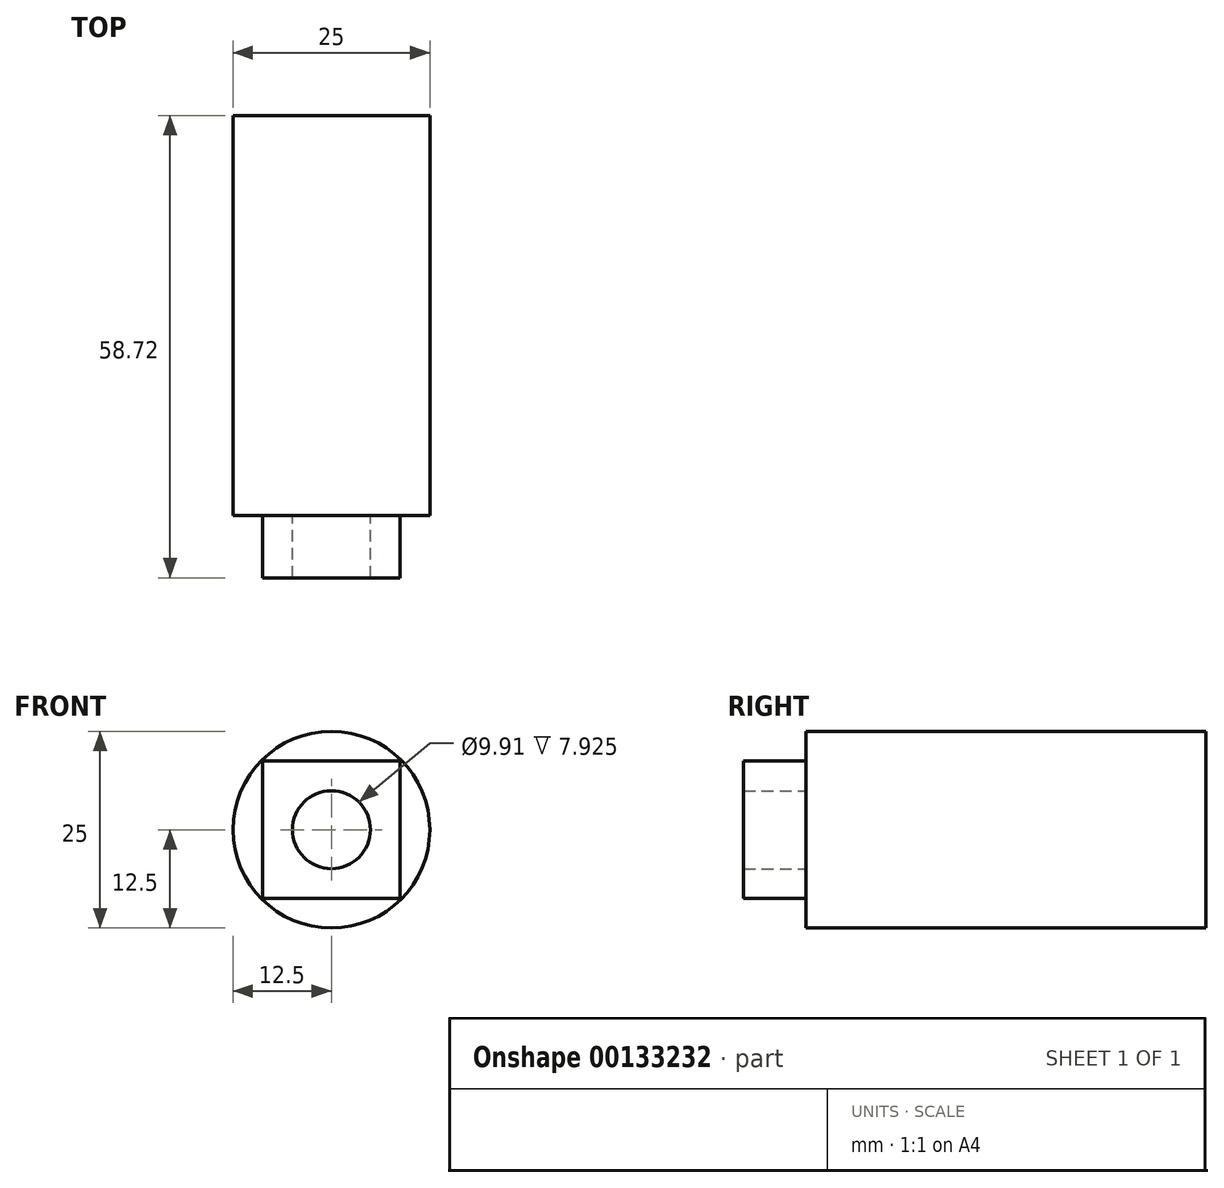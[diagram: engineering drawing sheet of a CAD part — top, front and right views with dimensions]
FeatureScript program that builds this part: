
annotation { "Feature Type Name" : "Feature", "Feature Type Description" : "" }
export const myFeature = defineFeature(function(context is Context, id is Id, definition is map)
    precondition{}
    {
        {
            var Q0;
            Q0=qCreatedBy(makeId("Front.planeOp"),FACE);
            var sketch = newSketch(context, id + "F0", { "sketchPlane" : qUnion([Q0])});
            skLineSegment(sketch, "E0.bottom", {"start": v(-8.72, 8.72) * mm, "end": v(8.72, 8.72) * mm});
            skLineSegment(sketch, "E0.top", {"start": v(-8.72, -8.72) * mm, "end": v(8.72, -8.72) * mm});
            skLineSegment(sketch, "E0.left", {"start": v(-8.72, 8.72) * mm, "end": v(-8.72, -8.72) * mm});
            skLineSegment(sketch, "E0.right", {"start": v(8.72, 8.72) * mm, "end": v(8.72, -8.72) * mm});
            skPoint(sketch, "E0.middle", {"position": v(0, 0) * mm});
            skCircle(sketch, "E1", {"center": v(0, 0) * mm, "radius": 12.5 * mm});
            skCircle(sketch, "E2", {"center": v(0, 0) * mm, "radius": 4.95 * mm});
            skSolve(sketch);
        }
        {
            var Q0;
            Q0=makeQuery(id+"F0.imprint","IMPRINT",FACE,{"disambiguationData":[TD([[makeQuery(id+"F0.imprint","IMPRINT",EDGE,{"derivedFrom":sQuery(id+"F0.wireOp",EDGE,"E2")}),1.0]])]});
            var Q1;
            Q1=makeQuery(id+"F0.imprint","IMPRINT",FACE,{"disambiguationData":[TD([[makeQuery(id+"F0.imprint","IMPRINT",EDGE,{"derivedFrom":sQuery(id+"F0.wireOp",EDGE,"E0.bottom")}),1.0]])]});
            var Q2;
            Q2=makeQuery(id+"F0.imprint","IMPRINT",FACE,{"disambiguationData":[TD([[makeQuery(id+"F0.imprint","IMPRINT",EDGE,{"derivedFrom":sQuery(id+"F0.wireOp",EDGE,"E0.bottom")}),-1.0]])]});
            extrude(context, id + "F1", {"entities" : qUnion([Q0, Q1, Q2]), "oppositeDirection" : true, "depth" : 50.8 * mm});
        }
        {
            var Q0;
            Q0=makeQuery(id+"F0.imprint","IMPRINT",FACE,{"disambiguationData":[TD([[makeQuery(id+"F0.imprint","IMPRINT",EDGE,{"derivedFrom":sQuery(id+"F0.wireOp",EDGE,"E0.bottom")}),-1.0]])]});
            extrude(context, id + "F2", {"entities" : qUnion([Q0]), "operationType" : NewBodyOperationType.ADD, "depth" : 7.92 * mm});
        }
    });
